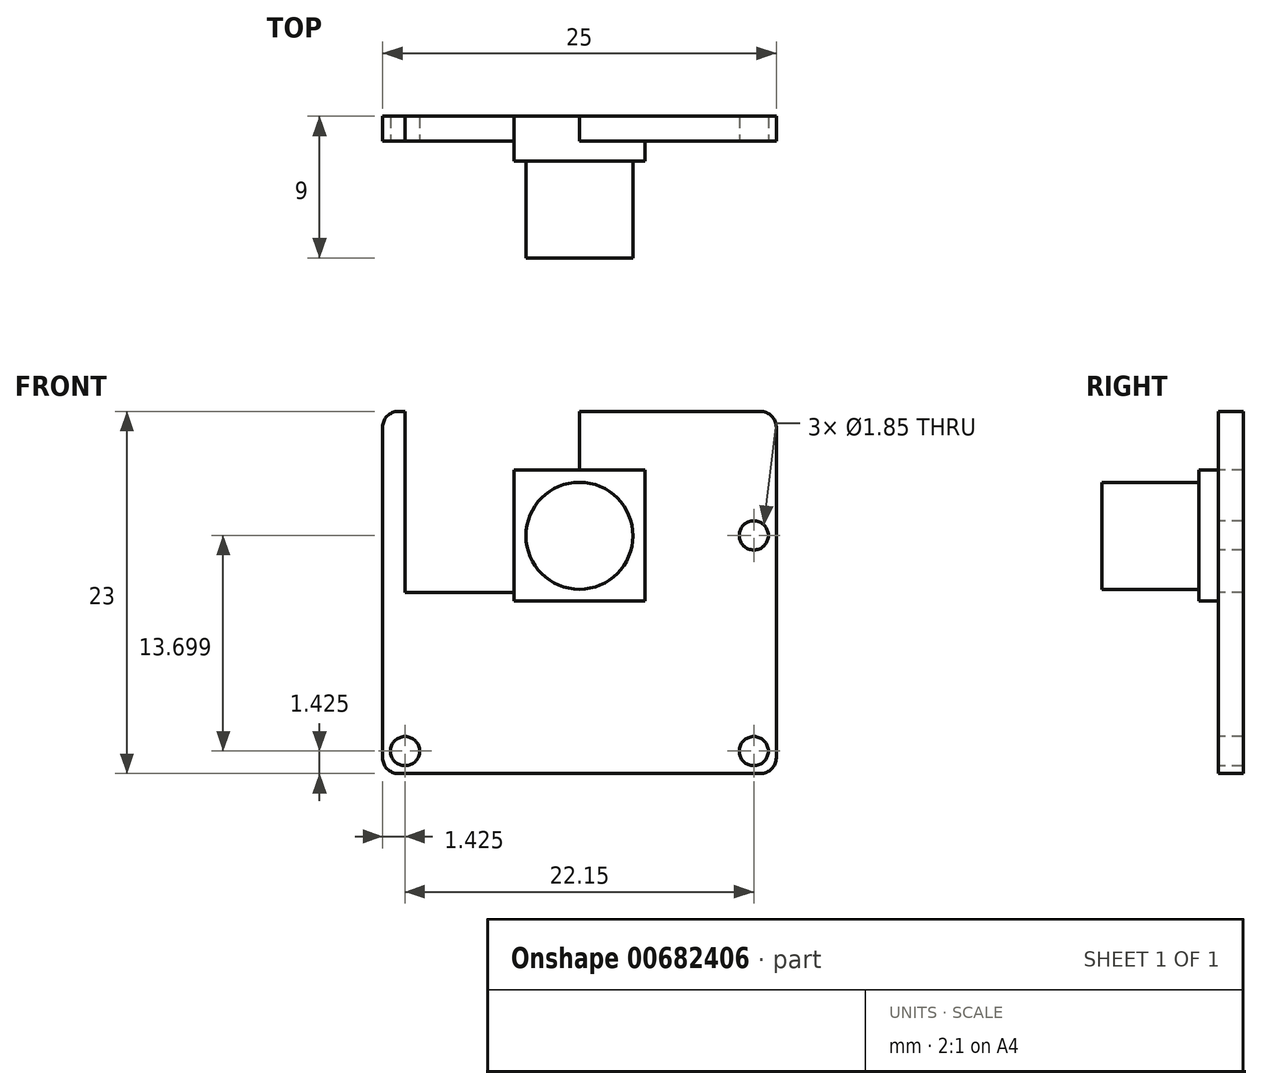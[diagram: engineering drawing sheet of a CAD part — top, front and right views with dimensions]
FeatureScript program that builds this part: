
annotation { "Feature Type Name" : "Feature", "Feature Type Description" : "" }
export const myFeature = defineFeature(function(context is Context, id is Id, definition is map)
    precondition{}
    {
        {
            var Q0;
            Q0=qCreatedBy(makeId("Front.planeOp"),FACE);
            var sketch = newSketch(context, id + "F0", { "sketchPlane" : qUnion([Q0])});
            skLineSegment(sketch, "E0.bottom", {"start": v(12.5, -11.5) * mm, "end": v(-12.5, -11.5) * mm});
            skLineSegment(sketch, "E0.top", {"start": v(12.5, 11.5) * mm, "end": v(-12.5, 11.5) * mm});
            skLineSegment(sketch, "E0.left", {"start": v(12.5, -11.5) * mm, "end": v(12.5, 11.5) * mm});
            skLineSegment(sketch, "E0.right", {"start": v(-12.5, -11.5) * mm, "end": v(-12.5, 11.5) * mm});
            skPoint(sketch, "E0.middle", {"position": v(0, 0) * mm});
            skSolve(sketch);
        }
        {
            var Q0;
            Q0=makeQuery(id+"F0.imprint","IMPRINT",FACE,{"disambiguationData":[TD([[makeQuery(id+"F0.imprint","IMPRINT",EDGE,{"derivedFrom":sQuery(id+"F0.wireOp",EDGE,"E0.bottom")}),-1.0]])]});
            extrude(context, id + "F1", {"entities" : qUnion([Q0]), "depth" : 1.59 * mm, "offsetDistance" : 25 * mm});
        }
        {
            var Q0;
            Q0=makeQuery(id+"F1.opExtrude","CAP_FACE",FACE,{"disambiguationData":[OSD([sQuery(id+"F0.wireOp",EDGE,"E0.bottom"),sQuery(id+"F0.wireOp",EDGE,"E0.top"),sQuery(id+"F0.wireOp",EDGE,"E0.left"),sQuery(id+"F0.wireOp",EDGE,"E0.right")])],"isStart":false});
            var sketch = newSketch(context, id + "F2", { "sketchPlane" : qUnion([Q0])});
            skLineSegment(sketch, "E1", {"start": v(0, 11.5) * mm, "end": v(0, -11.5) * mm});
            skLineSegment(sketch, "E2", {"start": v(-12.5, 0) * mm, "end": v(12.5, 0) * mm});
            skLineSegment(sketch, "E3.bottom", {"start": v(4.15, -0.53) * mm, "end": v(-4.15, -0.53) * mm});
            skLineSegment(sketch, "E3.top", {"start": v(4.15, 7.77) * mm, "end": v(-4.15, 7.77) * mm});
            skLineSegment(sketch, "E3.left", {"start": v(4.15, -0.53) * mm, "end": v(4.15, 7.77) * mm});
            skLineSegment(sketch, "E3.right", {"start": v(-4.15, -0.53) * mm, "end": v(-4.15, 7.77) * mm});
            skPoint(sketch, "E3.middle", {"position": v(0, 3.62) * mm});
            skLineSegment(sketch, "E4", {"start": v(-12.5, 3.62) * mm, "end": v(12.5, 3.62) * mm});
            skCircle(sketch, "E5", {"center": v(-11.08, -10.08) * mm, "radius": 0.93 * mm});
            skLineSegment(sketch, "E6", {"start": v(-12.5, -10.08) * mm, "end": v(12.5, -10.08) * mm});
            skCircle(sketch, "E7", {"center": v(11.07, -10.08) * mm, "radius": 0.93 * mm});
            skLineSegment(sketch, "E8", {"start": v(-11.08, -10.08) * mm, "end": v(-11.08, 11.5) * mm});
            skLineSegment(sketch, "E9", {"start": v(11.07, -10.08) * mm, "end": v(11.07, 11.5) * mm});
            skCircle(sketch, "E10", {"center": v(-11.08, 3.62) * mm, "radius": 0.8 * mm});
            skCircle(sketch, "E11", {"center": v(11.07, 3.62) * mm, "radius": 0.93 * mm});
            skSolve(sketch);
        }
        {
            var Q0;
            {var subQ0=sQuery(id+"F2.wireOp",EDGE,"E8");var subQ1=sQuery(id+"F2.wireOp",EDGE,"E4");var subQ2=makeQuery(id+"F2.imprint","INTERSECT",VERTEX,{"derivedFrom":[subQ1,subQ0]});Q0=makeQuery(id+"F2.imprint","IMPRINT",FACE,{"disambiguationData":[TD([[makeQuery(id+"F2.imprint","IMPRINT",EDGE,{"disambiguationData":[TD([[subQ2,-1.0]])],"derivedFrom":subQ1}),-1.0]])]});}
            var Q1;
            {var subQ0=sQuery(id+"F2.wireOp",EDGE,"E8");var subQ1=sQuery(id+"F2.wireOp",EDGE,"E4");var subQ2=makeQuery(id+"F2.imprint","INTERSECT",VERTEX,{"derivedFrom":[subQ1,subQ0]});Q1=makeQuery(id+"F2.imprint","IMPRINT",FACE,{"disambiguationData":[TD([[makeQuery(id+"F2.imprint","IMPRINT",EDGE,{"disambiguationData":[TD([[subQ2,-1.0]])],"derivedFrom":subQ1}),1.0]])]});}
            var Q2;
            {var subQ0=sQuery(id+"F2.wireOp",EDGE,"E10");var subQ1=sQuery(id+"F2.wireOp",EDGE,"E4");var subQ2=makeQuery(id+"F2.imprint","INTERSECT",VERTEX,{"disambiguationData":[OD(0.0)],"derivedFrom":[subQ1,subQ0]});Q2=makeQuery(id+"F2.imprint","IMPRINT",FACE,{"disambiguationData":[TD([[makeQuery(id+"F2.imprint","IMPRINT",EDGE,{"disambiguationData":[TD([[subQ2,-1.0]])],"derivedFrom":subQ1}),1.0]])]});}
            var Q3;
            {var subQ0=sQuery(id+"F2.wireOp",EDGE,"E10");var subQ1=sQuery(id+"F2.wireOp",EDGE,"E4");var subQ2=makeQuery(id+"F2.imprint","INTERSECT",VERTEX,{"disambiguationData":[OD(0.0)],"derivedFrom":[subQ1,subQ0]});Q3=makeQuery(id+"F2.imprint","IMPRINT",FACE,{"disambiguationData":[TD([[makeQuery(id+"F2.imprint","IMPRINT",EDGE,{"disambiguationData":[TD([[subQ2,-1.0]])],"derivedFrom":subQ1}),-1.0]])]});}
            var Q4;
            {var subQ0=sQuery(id+"F2.wireOp",EDGE,"E8");var subQ1=sQuery(id+"F2.wireOp",EDGE,"E5");var subQ2=makeQuery(id+"F2.imprint","INTERSECT",VERTEX,{"derivedFrom":[subQ1,subQ0]});Q4=makeQuery(id+"F2.imprint","IMPRINT",FACE,{"disambiguationData":[TD([[makeQuery(id+"F2.imprint","IMPRINT",EDGE,{"disambiguationData":[TD([[subQ2,-1.0]])],"derivedFrom":subQ1}),1.0]])]});}
            var Q5;
            {var subQ0=sQuery(id+"F2.wireOp",EDGE,"E8");var subQ1=sQuery(id+"F2.wireOp",EDGE,"E5");var subQ2=makeQuery(id+"F2.imprint","INTERSECT",VERTEX,{"derivedFrom":[subQ1,subQ0]});Q5=makeQuery(id+"F2.imprint","IMPRINT",FACE,{"disambiguationData":[TD([[makeQuery(id+"F2.imprint","IMPRINT",EDGE,{"disambiguationData":[TD([[subQ2,1.0]])],"derivedFrom":subQ1}),1.0]])]});}
            var Q6;
            {var subQ0=sQuery(id+"F2.wireOp",EDGE,"E6");var subQ1=sQuery(id+"F2.wireOp",EDGE,"E5");var subQ2=makeQuery(id+"F2.imprint","INTERSECT",VERTEX,{"disambiguationData":[OD(0.0)],"derivedFrom":[subQ1,subQ0]});Q6=makeQuery(id+"F2.imprint","IMPRINT",FACE,{"disambiguationData":[TD([[makeQuery(id+"F2.imprint","IMPRINT",EDGE,{"disambiguationData":[TD([[subQ2,1.0]])],"derivedFrom":subQ1}),1.0]])]});}
            var Q7;
            {var subQ0=sQuery(id+"F2.wireOp",EDGE,"E6");var subQ1=makeQuery(id+"F2.imprint","INTERSECT",VERTEX,{"derivedFrom":[subQ0,sQuery(id+"F2.wireOp",EDGE,"E9")]});Q7=makeQuery(id+"F2.imprint","IMPRINT",FACE,{"disambiguationData":[TD([[makeQuery(id+"F2.imprint","IMPRINT",EDGE,{"disambiguationData":[TD([[subQ1,1.0]])],"derivedFrom":subQ0}),-1.0]])]});}
            var Q8;
            {var subQ0=sQuery(id+"F2.wireOp",EDGE,"E9");var subQ1=sQuery(id+"F2.wireOp",EDGE,"E6");var subQ2=makeQuery(id+"F2.imprint","INTERSECT",VERTEX,{"derivedFrom":[subQ1,subQ0]});Q8=makeQuery(id+"F2.imprint","IMPRINT",FACE,{"disambiguationData":[TD([[makeQuery(id+"F2.imprint","IMPRINT",EDGE,{"disambiguationData":[TD([[subQ2,-1.0]])],"derivedFrom":subQ1}),1.0]])]});}
            var Q9;
            {var subQ0=sQuery(id+"F2.wireOp",EDGE,"E9");var subQ1=sQuery(id+"F2.wireOp",EDGE,"E6");var subQ2=makeQuery(id+"F2.imprint","INTERSECT",VERTEX,{"derivedFrom":[subQ1,subQ0]});Q9=makeQuery(id+"F2.imprint","IMPRINT",FACE,{"disambiguationData":[TD([[makeQuery(id+"F2.imprint","IMPRINT",EDGE,{"disambiguationData":[TD([[subQ2,1.0]])],"derivedFrom":subQ1}),1.0]])]});}
            var Q10;
            {var subQ0=sQuery(id+"F2.wireOp",EDGE,"E11");var subQ1=sQuery(id+"F2.wireOp",EDGE,"E4");var subQ2=makeQuery(id+"F2.imprint","INTERSECT",VERTEX,{"disambiguationData":[OD(0.0)],"derivedFrom":[subQ1,subQ0]});Q10=makeQuery(id+"F2.imprint","IMPRINT",FACE,{"disambiguationData":[TD([[makeQuery(id+"F2.imprint","IMPRINT",EDGE,{"disambiguationData":[TD([[subQ2,-1.0]])],"derivedFrom":subQ1}),-1.0]])]});}
            var Q11;
            {var subQ0=sQuery(id+"F2.wireOp",EDGE,"E9");var subQ1=sQuery(id+"F2.wireOp",EDGE,"E4");var subQ2=makeQuery(id+"F2.imprint","INTERSECT",VERTEX,{"derivedFrom":[subQ1,subQ0]});Q11=makeQuery(id+"F2.imprint","IMPRINT",FACE,{"disambiguationData":[TD([[makeQuery(id+"F2.imprint","IMPRINT",EDGE,{"disambiguationData":[TD([[subQ2,-1.0]])],"derivedFrom":subQ1}),1.0]])]});}
            var Q12;
            {var subQ0=sQuery(id+"F2.wireOp",EDGE,"E9");var subQ1=sQuery(id+"F2.wireOp",EDGE,"E4");var subQ2=makeQuery(id+"F2.imprint","INTERSECT",VERTEX,{"derivedFrom":[subQ1,subQ0]});Q12=makeQuery(id+"F2.imprint","IMPRINT",FACE,{"disambiguationData":[TD([[makeQuery(id+"F2.imprint","IMPRINT",EDGE,{"disambiguationData":[TD([[subQ2,-1.0]])],"derivedFrom":subQ1}),-1.0]])]});}
            var Q13;
            {var subQ0=sQuery(id+"F2.wireOp",EDGE,"E11");var subQ1=sQuery(id+"F2.wireOp",EDGE,"E4");var subQ2=makeQuery(id+"F2.imprint","INTERSECT",VERTEX,{"disambiguationData":[OD(0.0)],"derivedFrom":[subQ1,subQ0]});Q13=makeQuery(id+"F2.imprint","IMPRINT",FACE,{"disambiguationData":[TD([[makeQuery(id+"F2.imprint","IMPRINT",EDGE,{"disambiguationData":[TD([[subQ2,-1.0]])],"derivedFrom":subQ1}),1.0]])]});}
            extrude(context, id + "F3", {"entities" : qUnion([Q0, Q1, Q2, Q3, Q4, Q5, Q6, Q7, Q8, Q9, Q10, Q11, Q12, Q13]), "operationType" : NewBodyOperationType.REMOVE, "oppositeDirection" : true, "depth" : 25 * mm, "offsetDistance" : 25 * mm});
        }
        {
            var Q0;
            {var subQ0=sQuery(id+"F2.wireOp",EDGE,"E3.top");var subQ1=sQuery(id+"F2.wireOp",EDGE,"E1");var subQ2=makeQuery(id+"F2.imprint","INTERSECT",VERTEX,{"derivedFrom":[subQ1,subQ0]});Q0=makeQuery(id+"F2.imprint","IMPRINT",FACE,{"disambiguationData":[TD([[makeQuery(id+"F2.imprint","IMPRINT",EDGE,{"disambiguationData":[TD([[subQ2,-1.0]])],"derivedFrom":subQ1}),-1.0]])]});}
            var Q1;
            {var subQ0=sQuery(id+"F2.wireOp",EDGE,"E3.top");var subQ1=sQuery(id+"F2.wireOp",EDGE,"E1");var subQ2=makeQuery(id+"F2.imprint","INTERSECT",VERTEX,{"derivedFrom":[subQ1,subQ0]});Q1=makeQuery(id+"F2.imprint","IMPRINT",FACE,{"disambiguationData":[TD([[makeQuery(id+"F2.imprint","IMPRINT",EDGE,{"disambiguationData":[TD([[subQ2,-1.0]])],"derivedFrom":subQ1}),1.0]])]});}
            var Q2;
            {var subQ0=sQuery(id+"F2.wireOp",EDGE,"E4");var subQ1=sQuery(id+"F2.wireOp",EDGE,"E1");var subQ2=makeQuery(id+"F2.imprint","INTERSECT",VERTEX,{"derivedFrom":[subQ1,subQ0]});Q2=makeQuery(id+"F2.imprint","IMPRINT",FACE,{"disambiguationData":[TD([[makeQuery(id+"F2.imprint","IMPRINT",EDGE,{"disambiguationData":[TD([[subQ2,-1.0]])],"derivedFrom":subQ1}),1.0]])]});}
            var Q3;
            {var subQ0=sQuery(id+"F2.wireOp",EDGE,"E4");var subQ1=sQuery(id+"F2.wireOp",EDGE,"E1");var subQ2=makeQuery(id+"F2.imprint","INTERSECT",VERTEX,{"derivedFrom":[subQ1,subQ0]});Q3=makeQuery(id+"F2.imprint","IMPRINT",FACE,{"disambiguationData":[TD([[makeQuery(id+"F2.imprint","IMPRINT",EDGE,{"disambiguationData":[TD([[subQ2,-1.0]])],"derivedFrom":subQ1}),-1.0]])]});}
            var Q4;
            {var subQ0=sQuery(id+"F2.wireOp",EDGE,"E2");var subQ1=sQuery(id+"F2.wireOp",EDGE,"E1");var subQ2=makeQuery(id+"F2.imprint","INTERSECT",VERTEX,{"derivedFrom":[subQ1,subQ0]});Q4=makeQuery(id+"F2.imprint","IMPRINT",FACE,{"disambiguationData":[TD([[makeQuery(id+"F2.imprint","IMPRINT",EDGE,{"disambiguationData":[TD([[subQ2,-1.0]])],"derivedFrom":subQ1}),-1.0]])]});}
            var Q5;
            {var subQ0=sQuery(id+"F2.wireOp",EDGE,"E2");var subQ1=sQuery(id+"F2.wireOp",EDGE,"E1");var subQ2=makeQuery(id+"F2.imprint","INTERSECT",VERTEX,{"derivedFrom":[subQ1,subQ0]});Q5=makeQuery(id+"F2.imprint","IMPRINT",FACE,{"disambiguationData":[TD([[makeQuery(id+"F2.imprint","IMPRINT",EDGE,{"disambiguationData":[TD([[subQ2,-1.0]])],"derivedFrom":subQ1}),1.0]])]});}
            extrude(context, id + "F4", {"entities" : qUnion([Q0, Q1, Q2, Q3, Q4, Q5]), "operationType" : NewBodyOperationType.ADD, "depth" : 1.25 * mm, "offsetDistance" : 25 * mm});
        }
        {
            var Q0;
            Q0=makeQuery(id+"F4.opExtrude","CAP_FACE",FACE,{"disambiguationData":[OSD([sQuery(id+"F2.wireOp",EDGE,"E3.bottom"),sQuery(id+"F2.wireOp",EDGE,"E3.top"),sQuery(id+"F2.wireOp",EDGE,"E3.left"),sQuery(id+"F2.wireOp",EDGE,"E3.right")])],"isStart":false});
            var sketch = newSketch(context, id + "F5", { "sketchPlane" : qUnion([Q0])});
            skCircle(sketch, "E12", {"center": v(0, 3.6) * mm, "radius": 3.4 * mm});
            skSolve(sketch);
        }
        {
            var Q0;
            Q0=makeQuery(id+"F5.imprint","IMPRINT",FACE,{"disambiguationData":[TD([[makeQuery(id+"F5.imprint","IMPRINT",EDGE,{"derivedFrom":sQuery(id+"F5.wireOp",EDGE,"E12")}),1.0]])]});
            extrude(context, id + "F6", {"entities" : qUnion([Q0]), "operationType" : NewBodyOperationType.ADD, "depth" : 6.16 * mm, "offsetDistance" : 25 * mm});
        }
        {
            var Q0;
            Q0=makeQuery(id+"F1.opExtrude","SWEPT_EDGE",EDGE,{"disambiguationData":[OSD([sQuery(id+"F0.wireOp",EDGE,"E0.bottom"),sQuery(id+"F0.wireOp",EDGE,"E0.right")])]});
            var Q1;
            Q1=makeQuery(id+"F1.opExtrude","SWEPT_EDGE",EDGE,{"disambiguationData":[OSD([sQuery(id+"F0.wireOp",EDGE,"E0.top"),sQuery(id+"F0.wireOp",EDGE,"E0.right")])]});
            var Q2;
            Q2=makeQuery(id+"F1.opExtrude","SWEPT_EDGE",EDGE,{"disambiguationData":[OSD([sQuery(id+"F0.wireOp",EDGE,"E0.bottom"),sQuery(id+"F0.wireOp",EDGE,"E0.left")])]});
            var Q3;
            Q3=makeQuery(id+"F1.opExtrude","SWEPT_EDGE",EDGE,{"disambiguationData":[OSD([sQuery(id+"F0.wireOp",EDGE,"E0.top"),sQuery(id+"F0.wireOp",EDGE,"E0.left")])]});
            fillet(context, id + "F7", {"entities" : qUnion([Q0, Q1, Q2, Q3]), "radius" : 1 * mm, "tangentPropagation" : true, "allowEdgeOverflow" : false});
        }
    });
